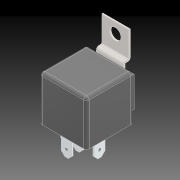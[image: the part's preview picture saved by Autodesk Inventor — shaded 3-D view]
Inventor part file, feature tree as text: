
AUTODESK INVENTOR PART (.ipt)
format: ipt  version: 2020 (Build 240168000, 168)  size: 540,160 bytes
history: mixed  units: mm
features: other x1, extrude x1, imported_body x1
ambient origin geometry x8: Origin, YZ Plane, XZ Plane, XY Plane, X Axis, Y Axis, Z Axis, Center Point
bodies: Body1 (imported_parasolid)
feature tree (3):
  other  "Твердое тело1"
  extrude  "Extrude8"  [1 undecoded]
  imported_body  NMx_Import_Brep_tag  [imported B-rep: ~23 faces, bbox_mm=[26.0, 23.5, 29.0]]
note: 1 required parameter value undecoded (feature->parameter linkage not recoverable at this tier; creation-order binding heuristic only, values carry confidence <= 0.55)
